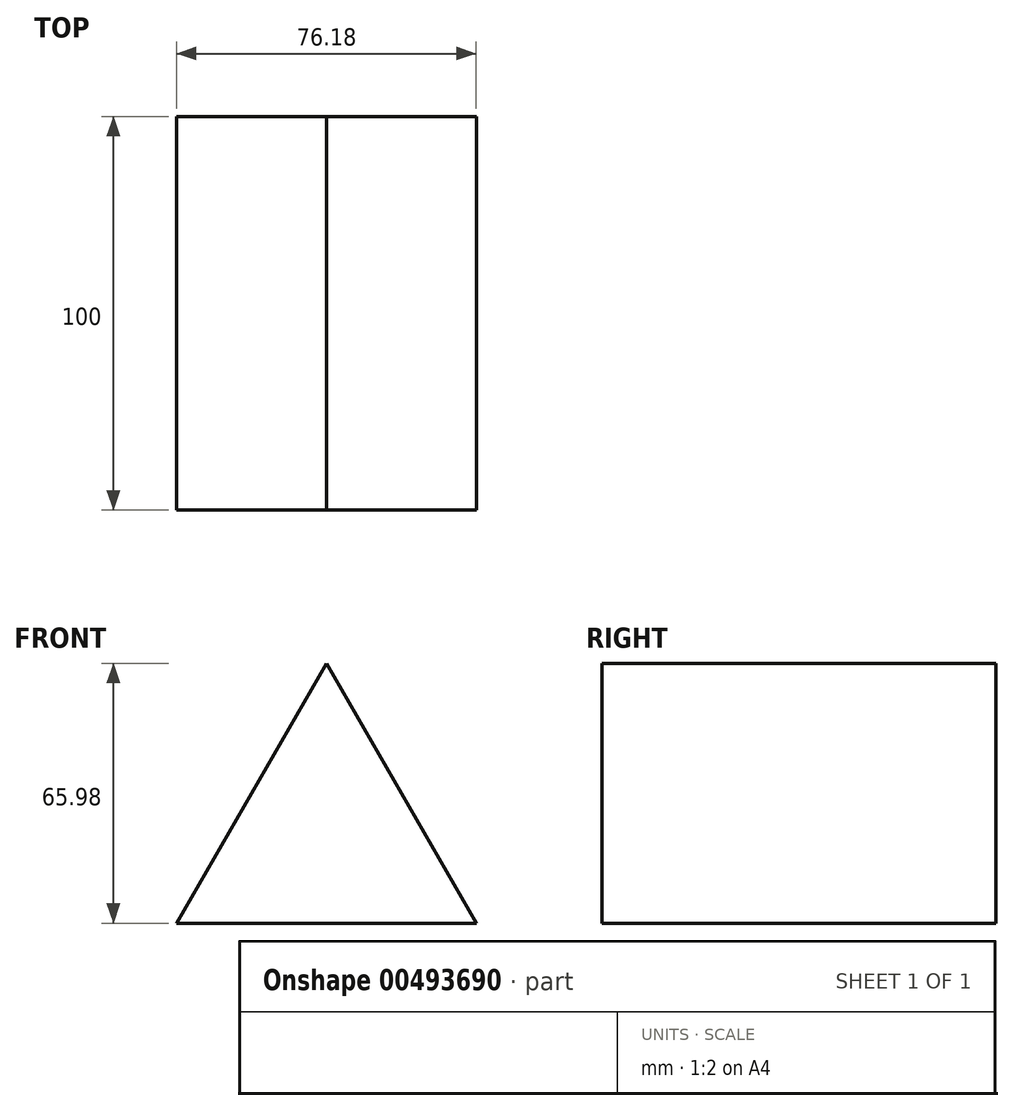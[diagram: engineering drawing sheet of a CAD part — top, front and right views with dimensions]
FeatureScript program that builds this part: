
annotation { "Feature Type Name" : "Feature", "Feature Type Description" : "" }
export const myFeature = defineFeature(function(context is Context, id is Id, definition is map)
    precondition{}
    {
        {
            var Q0;
            Q0=qCreatedBy(makeId("Front.planeOp"),FACE);
            var sketch = newSketch(context, id + "F0", { "sketchPlane" : qUnion([Q0])});
            skCircle(sketch, "E0.cCircle", {"center": v(0, 0) * mm, "radius": 43.99 * mm, "construction": true});
            skLineSegment(sketch, "E0.0", {"start": v(0, 43.99) * mm, "end": v(38.1, -22) * mm});
            skLineSegment(sketch, "E0.1", {"start": v(38.1, -22) * mm, "end": v(-38.1, -22) * mm});
            skLineSegment(sketch, "E0.2", {"start": v(-38.1, -22) * mm, "end": v(0, 43.99) * mm});
            skSolve(sketch);
        }
        {
            var Q0;
            Q0=makeQuery(id+"F0.imprint","IMPRINT",FACE,{"disambiguationData":[TD([[makeQuery(id+"F0.imprint","IMPRINT",EDGE,{"derivedFrom":sQuery(id+"F0.wireOp",EDGE,"E0.0")}),-1.0]])]});
            extrude(context, id + "F1", {"entities" : qUnion([Q0]), "depth" : 100 * mm});
        }
    });
